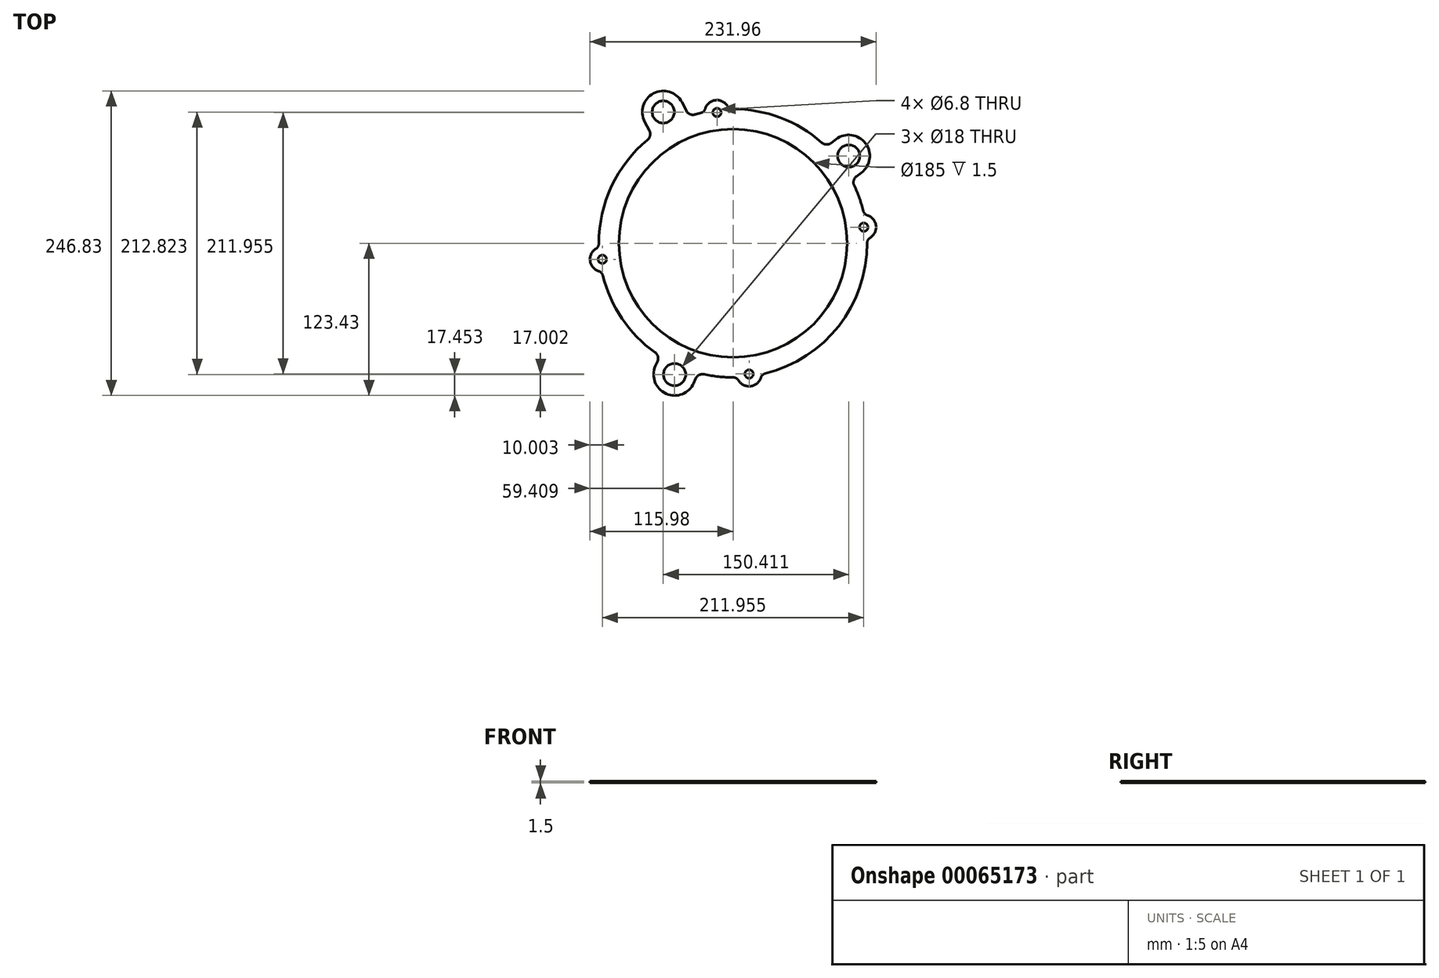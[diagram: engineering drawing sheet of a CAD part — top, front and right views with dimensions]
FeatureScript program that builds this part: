
annotation { "Feature Type Name" : "Feature", "Feature Type Description" : "" }
export const myFeature = defineFeature(function(context is Context, id is Id, definition is map)
    precondition{}
    {
        {
            var Q0;
            Q0=qCreatedBy(makeId("Top.planeOp"),FACE);
            var sketch = newSketch(context, id + "F0", { "sketchPlane" : qUnion([Q0])});
            skArc(sketch, "E0", {"start": v(-25.58, -99.26) * mm, "mid": v(-12.9, -101.69) * mm, "end": v(0, -102.5) * mm, "construction": true});
            skCircle(sketch, "E1", {"center": v(0, 0) * mm, "radius": 92.5 * mm});
            skLineSegment(sketch, "E2", {"start": v(0, 0) * mm, "end": v(-56.57, 106.4) * mm, "construction": true});
            skLineSegment(sketch, "E3", {"start": v(-71.58, 98.41) * mm, "end": v(-65.45, 86.88) * mm});
            skLineSegment(sketch, "E4", {"start": v(-41.56, 114.38) * mm, "end": v(-35.43, 102.84) * mm});
            skCircle(sketch, "E5", {"center": v(-56.57, 106.4) * mm, "radius": 9 * mm});
            skArc(sketch, "E6", {"start": v(-41.56, 114.38) * mm, "mid": v(-64.55, 121.4) * mm, "end": v(-71.58, 98.41) * mm});
            skLineSegment(sketch, "E7", {"start": v(0, 0) * mm, "end": v(93.84, 70.71) * mm, "construction": true});
            skArc(sketch, "E8", {"start": v(104.07, 57.14) * mm, "mid": v(107.42, 80.94) * mm, "end": v(83.6, 84.3) * mm});
            skCircle(sketch, "E9", {"center": v(93.84, 70.71) * mm, "radius": 9 * mm});
            skLineSegment(sketch, "E10", {"start": v(83.6, 84.3) * mm, "end": v(75.57, 78.23) * mm});
            skLineSegment(sketch, "E11", {"start": v(104.07, 57.14) * mm, "end": v(96.03, 51.08) * mm});
            skLineSegment(sketch, "E12", {"start": v(0, 0) * mm, "end": v(-47.38, -106.43) * mm, "construction": true});
            skArc(sketch, "E13", {"start": v(-62.92, -99.51) * mm, "mid": v(-54.3, -121.96) * mm, "end": v(-31.85, -113.34) * mm});
            skCircle(sketch, "E14", {"center": v(-47.38, -106.43) * mm, "radius": 9 * mm});
            skLineSegment(sketch, "E15", {"start": v(-62.92, -99.51) * mm, "end": v(-59.23, -91.23) * mm});
            skLineSegment(sketch, "E16", {"start": v(-31.85, -113.34) * mm, "end": v(-28.17, -105.06) * mm});
            skArc(sketch, "E17.trimOffspring", {"start": v(-62.46, 81.27) * mm, "mid": v(-72.2, 72.76) * mm, "end": v(-80.77, 63.1) * mm, "construction": true});
            skArc(sketch, "E18.trimOffspring", {"start": v(70.5, 74.4) * mm, "mid": v(37.94, 95.22) * mm, "end": v(0, 102.5) * mm, "construction": true});
            skLineSegment(sketch, "E19", {"start": v(0, 0) * mm, "end": v(-161.54, 126.21) * mm, "construction": true});
            skLineSegment(sketch, "E20", {"start": v(-13.01, 105.98) * mm, "end": v(-105.98, -13.01) * mm, "construction": true});
            skLineSegment(sketch, "E21", {"start": v(-13.01, 105.98) * mm, "end": v(105.98, 13.01) * mm, "construction": true});
            skLineSegment(sketch, "E22", {"start": v(105.98, 13.01) * mm, "end": v(13.01, -105.98) * mm, "construction": true});
            skLineSegment(sketch, "E23", {"start": v(13.01, -105.98) * mm, "end": v(-105.98, -13.01) * mm, "construction": true});
            skCircle(sketch, "E24", {"center": v(-105.98, -13.01) * mm, "radius": 3.4 * mm});
            skCircle(sketch, "E25", {"center": v(-13.01, 105.98) * mm, "radius": 3.4 * mm});
            skCircle(sketch, "E26", {"center": v(13.01, -105.98) * mm, "radius": 3.4 * mm});
            skCircle(sketch, "E27", {"center": v(105.98, 13.01) * mm, "radius": 3.4 * mm});
            skArc(sketch, "E28", {"start": v(-3.4, 108.72) * mm, "mid": v(-14.23, 115.9) * mm, "end": v(-23, 106.31) * mm});
            skArc(sketch, "E29", {"start": v(108.72, 3.4) * mm, "mid": v(115.9, 14.23) * mm, "end": v(106.31, 23) * mm});
            skArc(sketch, "E30", {"start": v(-108.72, -3.4) * mm, "mid": v(-115.9, -14.23) * mm, "end": v(-106.31, -23) * mm});
            skArc(sketch, "E31", {"start": v(3.4, -108.72) * mm, "mid": v(14.23, -115.9) * mm, "end": v(23, -106.31) * mm});
            skLineSegment(sketch, "E32", {"start": v(0, 0) * mm, "end": v(-13.01, 105.98) * mm, "construction": true});
            skLineSegment(sketch, "E33", {"start": v(0, 0) * mm, "end": v(105.98, 13.01) * mm, "construction": true});
            skLineSegment(sketch, "E34", {"start": v(13.01, -105.98) * mm, "end": v(0, 0) * mm, "construction": true});
            skLineSegment(sketch, "E35", {"start": v(-105.98, -13.01) * mm, "end": v(0, 0) * mm, "construction": true});
            skArc(sketch, "E36.trimOffspring", {"start": v(0, -102.5) * mm, "mid": v(72.48, -72.48) * mm, "end": v(102.5, 0) * mm, "construction": true});
            skArc(sketch, "E37.trimOffspring", {"start": v(-80.77, 63.1) * mm, "mid": v(-101.17, -16.43) * mm, "end": v(-56.64, -85.43) * mm, "construction": true});
            skArc(sketch, "E38.trimOffspring", {"start": v(102.5, 0) * mm, "mid": v(99.57, 24.32) * mm, "end": v(90.96, 47.25) * mm, "construction": true});
            skArc(sketch, "E39.trimOffspring", {"start": v(0, 102.5) * mm, "mid": v(-16.43, 101.17) * mm, "end": v(-32.44, 97.23) * mm, "construction": true});
            skArc(sketch, "E40", {"start": v(-65.45, 86.88) * mm, "mid": v(-98.09, 47.02) * mm, "end": v(-108.72, -3.4) * mm});
            skArc(sketch, "E41.trimOffspring", {"start": v(-23, 106.31) * mm, "mid": v(-29.27, 104.76) * mm, "end": v(-35.43, 102.84) * mm});
            skArc(sketch, "E42.trimOffspring", {"start": v(75.57, 78.23) * mm, "mid": v(39.18, 101.47) * mm, "end": v(-3.4, 108.72) * mm});
            skArc(sketch, "E43.trimOffspring", {"start": v(-106.31, -23) * mm, "mid": v(-89.52, -61.78) * mm, "end": v(-59.23, -91.23) * mm});
            skArc(sketch, "E44.trimOffspring", {"start": v(-28.17, -105.06) * mm, "mid": v(-12.52, -108.05) * mm, "end": v(3.4, -108.72) * mm});
            skArc(sketch, "E45.trimOffspring", {"start": v(23, -106.31) * mm, "mid": v(85.71, -66.97) * mm, "end": v(108.72, 3.4) * mm});
            skArc(sketch, "E46.trimOffspring", {"start": v(106.31, 23) * mm, "mid": v(102.14, 37.4) * mm, "end": v(96.03, 51.08) * mm});
            skSolve(sketch);
        }
        {
            var Q0;
            Q0 = qSketchRegion(id + "F0", true);
            extrude(context, id + "F1", {"entities" : qUnion([Q0]), "depth" : 1.5 * mm});
        }
        {
            var Q0;
            Q0=makeQuery(id+"F1.opExtrude","SWEPT_EDGE",EDGE,{"disambiguationData":[OSD([sQuery(id+"F0.wireOp",EDGE,"E4"),sQuery(id+"F0.wireOp",EDGE,"E39.trimOffspring")])]});
            var Q1;
            Q1=makeQuery(id+"F1.opExtrude","SWEPT_EDGE",EDGE,{"disambiguationData":[OSD([sQuery(id+"F0.wireOp",EDGE,"E18.trimOffspring"),sQuery(id+"F0.wireOp",EDGE,"ya3MsAB2-q0bt-jmvW-aNfu-D74RWQP9sr7h")])]});
            var Q2;
            Q2=makeQuery(id+"F1.opExtrude","SWEPT_EDGE",EDGE,{"disambiguationData":[OSD([sQuery(id+"F0.wireOp",EDGE,"fd1MxPNi-SQlp-5HdN-JMCP-74l2m2HyWusR"),sQuery(id+"F0.wireOp",EDGE,"E39.trimOffspring")])]});
            var Q3;
            Q3=makeQuery(id+"F1.opExtrude","SWEPT_EDGE",EDGE,{"disambiguationData":[OSD([sQuery(id+"F0.wireOp",EDGE,"E10"),sQuery(id+"F0.wireOp",EDGE,"E18.trimOffspring")])]});
            var Q4;
            Q4=makeQuery(id+"F1.opExtrude","SWEPT_EDGE",EDGE,{"disambiguationData":[OSD([sQuery(id+"F0.wireOp",EDGE,"E11"),sQuery(id+"F0.wireOp",EDGE,"E38.trimOffspring")])]});
            var Q5;
            Q5=makeQuery(id+"F1.opExtrude","SWEPT_EDGE",EDGE,{"disambiguationData":[OSD([sQuery(id+"F0.wireOp",EDGE,"WZ5NBzJ6-mwVv-dQXb-De6L-Gc0HqvJz0B2o"),sQuery(id+"F0.wireOp",EDGE,"E36.trimOffspring")])]});
            var Q6;
            Q6=makeQuery(id+"F1.opExtrude","SWEPT_EDGE",EDGE,{"disambiguationData":[OSD([sQuery(id+"F0.wireOp",EDGE,"c30rzbwY-d2mc-YhG8-muqe-wVkuMSDvb014"),sQuery(id+"F0.wireOp",EDGE,"E38.trimOffspring")])]});
            var Q7;
            Q7=makeQuery(id+"F1.opExtrude","SWEPT_EDGE",EDGE,{"disambiguationData":[OSD([sQuery(id+"F0.wireOp",EDGE,"FoWTM66R-kaa3-fbvY-cmHq-0JX1xwPYWUB1"),sQuery(id+"F0.wireOp",EDGE,"E36.trimOffspring")])]});
            var Q8;
            Q8=makeQuery(id+"F1.opExtrude","SWEPT_EDGE",EDGE,{"disambiguationData":[OSD([sQuery(id+"F0.wireOp",EDGE,"E0"),sQuery(id+"F0.wireOp",EDGE,"IZypz9Dj-osBE-cMbL-xxfH-czBpjC94OlnO")])]});
            var Q9;
            Q9=makeQuery(id+"F1.opExtrude","SWEPT_EDGE",EDGE,{"disambiguationData":[OSD([sQuery(id+"F0.wireOp",EDGE,"E15"),sQuery(id+"F0.wireOp",EDGE,"E37.trimOffspring")])]});
            var Q10;
            Q10=makeQuery(id+"F1.opExtrude","SWEPT_EDGE",EDGE,{"disambiguationData":[OSD([sQuery(id+"F0.wireOp",EDGE,"E0"),sQuery(id+"F0.wireOp",EDGE,"E16")])]});
            var Q11;
            Q11=makeQuery(id+"F1.opExtrude","SWEPT_EDGE",EDGE,{"disambiguationData":[OSD([sQuery(id+"F0.wireOp",EDGE,"E17.trimOffspring"),sQuery(id+"F0.wireOp",EDGE,"F8pXuhb9-NOzJ-zVP4-HWFb-zKhPtgqAt5MS")])]});
            var Q12;
            Q12=makeQuery(id+"F1.opExtrude","SWEPT_EDGE",EDGE,{"disambiguationData":[OSD([sQuery(id+"F0.wireOp",EDGE,"ShpCb5aW-UkPn-bsId-yUAQ-1v0htIeXeI6Q"),sQuery(id+"F0.wireOp",EDGE,"E37.trimOffspring")])]});
            var Q13;
            Q13=makeQuery(id+"F1.opExtrude","SWEPT_EDGE",EDGE,{"disambiguationData":[OSD([sQuery(id+"F0.wireOp",EDGE,"E3"),sQuery(id+"F0.wireOp",EDGE,"E17.trimOffspring")])]});
            fillet(context, id + "F2", {"entities" : qUnion([Q0, Q1, Q2, Q3, Q4, Q5, Q6, Q7, Q8, Q9, Q10, Q11, Q12, Q13]), "radius" : 6 * mm, "tangentPropagation" : true, "allowEdgeOverflow" : false});
        }
        {
            var Q0;
            {var subQ0=sQuery(id+"F0.wireOp",EDGE,"E40");var subQ1=sQuery(id+"F0.wireOp",EDGE,"E28");Q0=makeQuery(id+"F1.opExtrude","SWEPT_EDGE",EDGE,{"disambiguationData":[OSD([subQ1,subQ0]),TDD([makeQuery(id+"F0.imprint","INTERSECT",VERTEX,{"disambiguationData":[OD(0.0)],"derivedFrom":[subQ1,subQ0]})])]});}
            var Q1;
            {var subQ0=sQuery(id+"F0.wireOp",EDGE,"E40");var subQ1=sQuery(id+"F0.wireOp",EDGE,"E28");Q1=makeQuery(id+"F1.opExtrude","SWEPT_EDGE",EDGE,{"disambiguationData":[OSD([subQ1,subQ0]),TDD([makeQuery(id+"F0.imprint","INTERSECT",VERTEX,{"disambiguationData":[OD(1.0)],"derivedFrom":[subQ1,subQ0]})])]});}
            var Q2;
            {var subQ0=sQuery(id+"F0.wireOp",EDGE,"E40");var subQ1=sQuery(id+"F0.wireOp",EDGE,"E29");Q2=makeQuery(id+"F1.opExtrude","SWEPT_EDGE",EDGE,{"disambiguationData":[OSD([subQ1,subQ0]),TDD([makeQuery(id+"F0.imprint","INTERSECT",VERTEX,{"disambiguationData":[OD(1.0)],"derivedFrom":[subQ1,subQ0]})])]});}
            var Q3;
            {var subQ0=sQuery(id+"F0.wireOp",EDGE,"E40");var subQ1=sQuery(id+"F0.wireOp",EDGE,"E29");Q3=makeQuery(id+"F1.opExtrude","SWEPT_EDGE",EDGE,{"disambiguationData":[OSD([subQ1,subQ0]),TDD([makeQuery(id+"F0.imprint","INTERSECT",VERTEX,{"disambiguationData":[OD(0.0)],"derivedFrom":[subQ1,subQ0]})])]});}
            var Q4;
            {var subQ0=sQuery(id+"F0.wireOp",EDGE,"E40");var subQ1=sQuery(id+"F0.wireOp",EDGE,"E31");Q4=makeQuery(id+"F1.opExtrude","SWEPT_EDGE",EDGE,{"disambiguationData":[OSD([subQ1,subQ0]),TDD([makeQuery(id+"F0.imprint","INTERSECT",VERTEX,{"disambiguationData":[OD(1.0)],"derivedFrom":[subQ1,subQ0]})])]});}
            var Q5;
            {var subQ0=sQuery(id+"F0.wireOp",EDGE,"E40");var subQ1=sQuery(id+"F0.wireOp",EDGE,"E31");Q5=makeQuery(id+"F1.opExtrude","SWEPT_EDGE",EDGE,{"disambiguationData":[OSD([subQ1,subQ0]),TDD([makeQuery(id+"F0.imprint","INTERSECT",VERTEX,{"disambiguationData":[OD(0.0)],"derivedFrom":[subQ1,subQ0]})])]});}
            var Q6;
            {var subQ0=sQuery(id+"F0.wireOp",EDGE,"E40");var subQ1=sQuery(id+"F0.wireOp",EDGE,"E30");Q6=makeQuery(id+"F1.opExtrude","SWEPT_EDGE",EDGE,{"disambiguationData":[OSD([subQ1,subQ0]),TDD([makeQuery(id+"F0.imprint","INTERSECT",VERTEX,{"disambiguationData":[OD(0.0)],"derivedFrom":[subQ1,subQ0]})])]});}
            var Q7;
            {var subQ0=sQuery(id+"F0.wireOp",EDGE,"E40");var subQ1=sQuery(id+"F0.wireOp",EDGE,"E30");Q7=makeQuery(id+"F1.opExtrude","SWEPT_EDGE",EDGE,{"disambiguationData":[OSD([subQ1,subQ0]),TDD([makeQuery(id+"F0.imprint","INTERSECT",VERTEX,{"disambiguationData":[OD(1.0)],"derivedFrom":[subQ1,subQ0]})])]});}
            var Q8;
            Q8=makeQuery(id+"F1.opExtrude","SWEPT_EDGE",EDGE,{"disambiguationData":[OSD([sQuery(id+"F0.wireOp",EDGE,"E30"),sQuery(id+"F0.wireOp",EDGE,"E43.trimOffspring")])]});
            fillet(context, id + "F3", {"entities" : qUnion([Q0, Q1, Q2, Q3, Q4, Q5, Q6, Q7, Q8]), "radius" : 5 * mm, "tangentPropagation" : true, "allowEdgeOverflow" : false});
        }
    });
